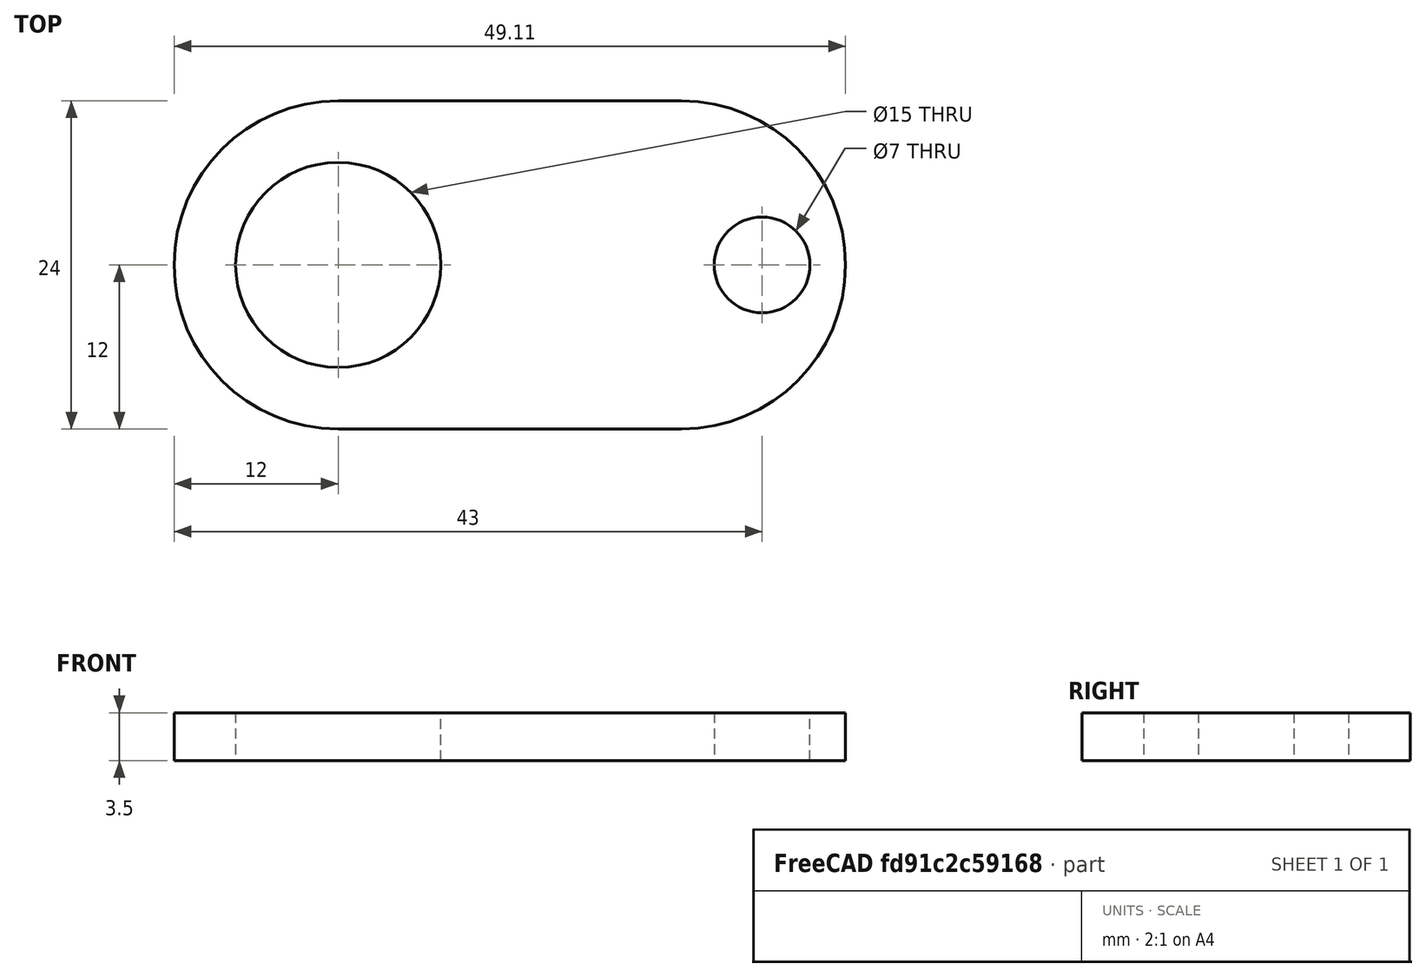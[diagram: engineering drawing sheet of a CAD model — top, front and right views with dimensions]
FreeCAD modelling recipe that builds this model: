
FCSTD DOCUMENT  (FreeCAD 0.16R)
Label: CrankSpacer3.5mm31mm
License: All rights reserved
LicenseURL: http://en.wikipedia.org/wiki/All_rights_reserved
objects: Sketcher::SketchObject×1, PartDesign::Pad×1, Mesh::Feature×1
note: 3 computed .brp shape members not serialized (recipe doc carries the construction recipe); baked Part::Feature solids carry a one-line shape summary decoded from their .brp

FEATURE [Sketcher::SketchObject] Sketch
  sketch-geometry (6):
    g0: Circle CenterX=0 CenterY=0 CenterZ=0 NormalX=0 NormalY=0 NormalZ=1 Radius=7.5
    g1: ArcOfCircle CenterX=0 CenterY=0 CenterZ=0 NormalX=0 NormalY=0 NormalZ=1 Radius=12 StartAngle=1.5708 EndAngle=4.71239
    g2: ArcOfCircle CenterX=25.1077 CenterY=0 CenterZ=0 NormalX=0 NormalY=0 NormalZ=1 Radius=12 StartAngle=4.71239 EndAngle=7.85398
    g3: LineSegment StartX=0 StartY=-12 StartZ=0 EndX=25.1077 EndY=-12 EndZ=0
    g4: LineSegment StartX=0 StartY=12 StartZ=0 EndX=25.1077 EndY=12 EndZ=0
    g5: Circle CenterX=31 CenterY=0 CenterZ=0 NormalX=0 NormalY=0 NormalZ=1 Radius=3.5
  constraints (13):
    c: Coincident(g0,g-1)
    c: Radius(g0) = 7.5
    c: Tangent(g1,g4) = 1.5708
    c: Tangent(g1,g3) = -1.5708
    c: Tangent(g3,g2) = -1.5708
    c: Tangent(g4,g2) = 1.5708
    c: Horizontal(g3)
    c: Equal(g1,g2)
    c: Coincident(g1,g-1)
    c: DistanceY(g1) = 12
    c: DistanceX(g5) = 31
    c: Radius(g5) = 3.5
    c: PointOnObject(g5,g-1)
FEATURE [PartDesign::Pad] Pad
  Length = 3.5
  Length2 = 100
  Sketch = -> Sketch
  Type = 0
FEATURE [Mesh::Feature] Mesh  label="Pad (Meshed)"
